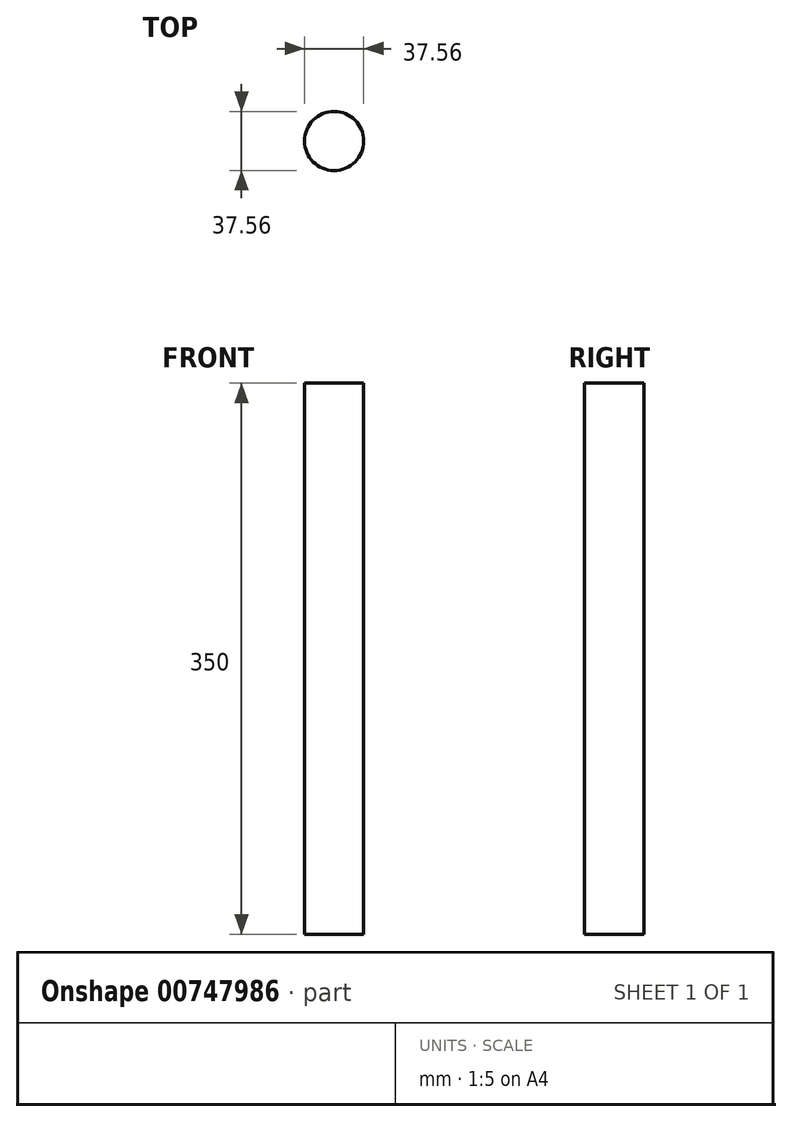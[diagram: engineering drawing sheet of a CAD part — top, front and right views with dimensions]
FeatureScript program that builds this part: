
annotation { "Feature Type Name" : "Feature", "Feature Type Description" : "" }
export const myFeature = defineFeature(function(context is Context, id is Id, definition is map)
    precondition{}
    {
        {
            var Q0;
            Q0=qCreatedBy(makeId("Top.planeOp"),FACE);
            var sketch = newSketch(context, id + "F0", { "sketchPlane" : qUnion([Q0])});
            skCircle(sketch, "E0", {"center": v(0, 0) * mm, "radius": 18.78 * mm});
            skSolve(sketch);
        }
        {
            var Q0;
            Q0=makeQuery(id+"F0.imprint","IMPRINT",FACE,{"disambiguationData":[TD([[makeQuery(id+"F0.imprint","IMPRINT",EDGE,{"derivedFrom":sQuery(id+"F0.wireOp",EDGE,"E0")}),1.0]])]});
            extrude(context, id + "F1", {"entities" : qUnion([Q0]), "endBound" : BoundingType.SYMMETRIC, "depth" : 350 * mm, "offsetDistance" : 25 * mm});
        }
    });
